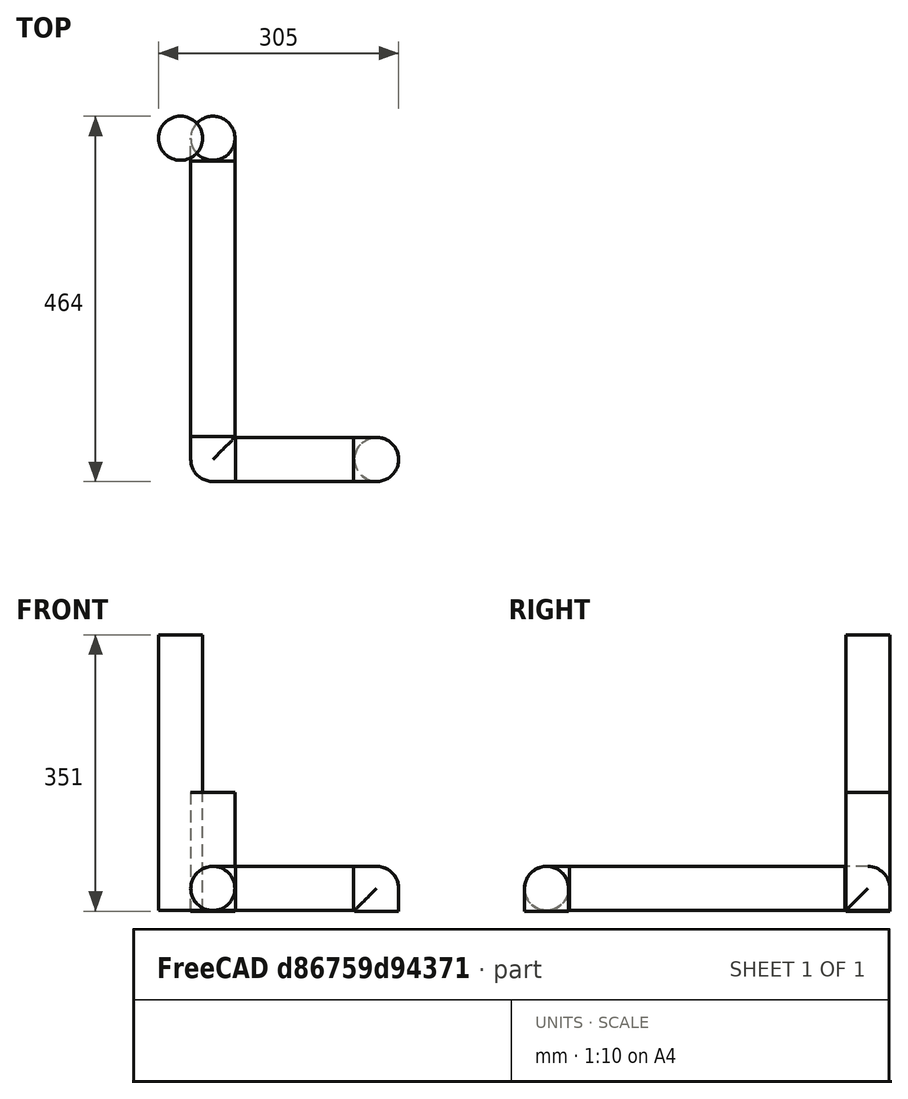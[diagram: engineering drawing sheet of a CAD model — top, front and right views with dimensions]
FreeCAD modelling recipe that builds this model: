
FCSTD DOCUMENT  (FreeCAD 0.21R33668 +26 (Git))
Label: arm-L1
License: All rights reserved
LicenseURL: http://en.wikipedia.org/wiki/All_rights_reserved
objects: App::FeaturePython×8, Part::FeaturePython×5, Part::Cylinder×2, App::Part×1
note: 7 computed .brp shape members not serialized (recipe doc carries the construction recipe); baked Part::Feature solids carry a one-line shape summary decoded from their .brp

FEATURE [Part::Cylinder] Cylinder002
  Angle = 360
  AttacherType = Attacher::AttachEngine3D
  FirstAngle = 0
  Height = 350
  Placement = pos=(-41,0,0) rot=(90,0,1;0rad)
  Radius = 28
  SecondAngle = 0
FEATURE [Part::FeaturePython] b_arm_subpart_angle_001_002  label="arm-subpart-angle"  # a2plus imported part (geometry in sourceFile) (typed FeaturePython)
  Placement = pos=(0,0,0) rot=(0.57735,-0.57735,0.57735;2.0944rad)
  a2p_Version = 0.4.60i
  fixedPosition = true
  objectType = a2pPart
  sourceFile = .\arm-subpart-angle.FCStd
  subassemblyImport = false
  timeLastImport = 1.69953e+09
  updateColors = true
FEATURE [Part::FeaturePython] Cylinder002_001  # a2plus imported part (geometry in sourceFile) (typed FeaturePython)
  Placement = pos=(-40.6444,-29,33.3885) rot=(0.046618,-0.706338,0.706338;3.04842rad)
  a2p_Version = 0.4.60i
  fixedPosition = false
  localSourceObject = Cylinder002
  objectType = a2pPart
  sourceFile = converted
  subassemblyImport = false
  timeLastImport = 1.69953e+09
  updateColors = true
FEATURE [Part::Cylinder] Cylinder
  Angle = 360
  AttacherType = Attacher::AttachEngine3D
  FirstAngle = 0
  Height = 150
  Radius = 28
  SecondAngle = 0
FEATURE [Part::FeaturePython] Cylinder_001  # a2plus imported part (geometry in sourceFile) (typed FeaturePython)
  Placement = pos=(179,-408,28) rot=(0.601329,-0.526124,-0.601329;2.17294rad)
  a2p_Version = 0.4.60i
  fixedPosition = false
  localSourceObject = Cylinder
  objectType = a2pPart
  sourceFile = converted
  subassemblyImport = false
  timeLastImport = 1.69953e+09
  updateColors = true
FEATURE [Part::FeaturePython] b_arm_subpart_angle_001_003  label="arm-subpart-angle001"  # a2plus imported part (geometry in sourceFile) (typed FeaturePython)
  Placement = pos=(3.80866e-05,-380,28) rot=(-0.57735,0.57735,-0.57735;2.0944rad)
  a2p_Version = 0.4.60i
  fixedPosition = false
  objectType = a2pPart
  sourceFile = .\arm-subpart-angle.FCStd
  subassemblyImport = false
  timeLastImport = 1.69953e+09
  updateColors = true
FEATURE [Part::FeaturePython] b_arm_subpart_angle_001_004  label="arm-subpart-angle002"  # a2plus imported part (geometry in sourceFile) (typed FeaturePython)
  Placement = pos=(208,-408,2.4919e-09) rot=(0,-1,0;1.5708rad)
  a2p_Version = 0.4.60i
  fixedPosition = false
  objectType = a2pPart
  sourceFile = .\arm-subpart-angle.FCStd
  subassemblyImport = false
  timeLastImport = 1.69953e+09
  updateColors = true
FEATURE [App::FeaturePython] centerOfMass_001  label="centerOfMass_001__arm-subpart-angle"  # a2plus constraint (typed FeaturePython)
  Object1 = Cylinder002_001
  Object2 = b_arm_subpart_angle_001_002
  ParentTreeObject = -> Cylinder002_001
  SubElement1 = Face2
  SubElement2 = Face6
  Suppressed = false
  Type = CenterOfMass
  directionConstraint = 0
  lockRotation = true
  offset = 0
FEATURE [App::FeaturePython] centerOfMass_001_mirror  label="centerOfMass_001__Cylinder002_001"  # a2plus constraint (typed FeaturePython)
  Object1 = Cylinder002_001
  Object2 = b_arm_subpart_angle_001_002
  ParentTreeObject = -> b_arm_subpart_angle_001_002
  SubElement1 = Face2
  SubElement2 = Face6
  Suppressed = false
  Type = CenterOfMass
  directionConstraint = 0
  lockRotation = true
  offset = 0
FEATURE [App::FeaturePython] centerOfMass_002  label="centerOfMass_002__arm-subpart-angle001"  # a2plus constraint (typed FeaturePython)
  Object1 = Cylinder002_001
  Object2 = b_arm_subpart_angle_001_003
  ParentTreeObject = -> Cylinder002_001
  SubElement1 = Face3
  SubElement2 = Face5
  Suppressed = false
  Type = CenterOfMass
  directionConstraint = 1
  lockRotation = true
  offset = 0
FEATURE [App::FeaturePython] centerOfMass_002_mirror  label="centerOfMass_002__Cylinder002_001"  # a2plus constraint (typed FeaturePython)
  Object1 = Cylinder002_001
  Object2 = b_arm_subpart_angle_001_003
  ParentTreeObject = -> b_arm_subpart_angle_001_003
  SubElement1 = Face3
  SubElement2 = Face5
  Suppressed = false
  Type = CenterOfMass
  directionConstraint = 1
  lockRotation = true
  offset = 0
FEATURE [App::FeaturePython] centerOfMass_003  label="centerOfMass_003__arm-subpart-angle001"  # a2plus constraint (typed FeaturePython)
  Object1 = Cylinder_001
  Object2 = b_arm_subpart_angle_001_003
  ParentTreeObject = -> Cylinder_001
  SubElement1 = Face3
  SubElement2 = Face6
  Suppressed = false
  Type = CenterOfMass
  directionConstraint = 1
  lockRotation = true
  offset = 0
FEATURE [App::FeaturePython] centerOfMass_003_mirror  label="centerOfMass_003__Cylinder_001"  # a2plus constraint (typed FeaturePython)
  Object1 = Cylinder_001
  Object2 = b_arm_subpart_angle_001_003
  ParentTreeObject = -> b_arm_subpart_angle_001_003
  SubElement1 = Face3
  SubElement2 = Face6
  Suppressed = false
  Type = CenterOfMass
  directionConstraint = 1
  lockRotation = true
  offset = 0
FEATURE [App::FeaturePython] centerOfMass_004  label="centerOfMass_004__arm-subpart-angle002"  # a2plus constraint (typed FeaturePython)
  Object1 = Cylinder_001
  Object2 = b_arm_subpart_angle_001_004
  ParentTreeObject = -> Cylinder_001
  SubElement1 = Face2
  SubElement2 = Face6
  Suppressed = false
  Type = CenterOfMass
  directionConstraint = 0
  lockRotation = true
  offset = 0
FEATURE [App::FeaturePython] centerOfMass_004_mirror  label="centerOfMass_004__Cylinder_001"  # a2plus constraint (typed FeaturePython)
  Object1 = Cylinder_001
  Object2 = b_arm_subpart_angle_001_004
  ParentTreeObject = -> b_arm_subpart_angle_001_004
  SubElement1 = Face2
  SubElement2 = Face6
  Suppressed = false
  Type = CenterOfMass
  directionConstraint = 0
  lockRotation = true
  offset = 0
FEATURE [App::Part] Part
  Group = -> [centerOfMass_001_mirror,b_arm_subpart_angle_001_002,centerOfMass_002,centerOfMass_001,Cylinder002_001,centerOfMass_003,centerOfMass_004,Cylinder_001,centerOfMass_002_mirror,centerOfMass_003_mirror,b_arm_subpart_angle_001_003,centerOfMass_004_mirror,b_arm_subpart_angle_001_004]
  Origin = -> Origin
